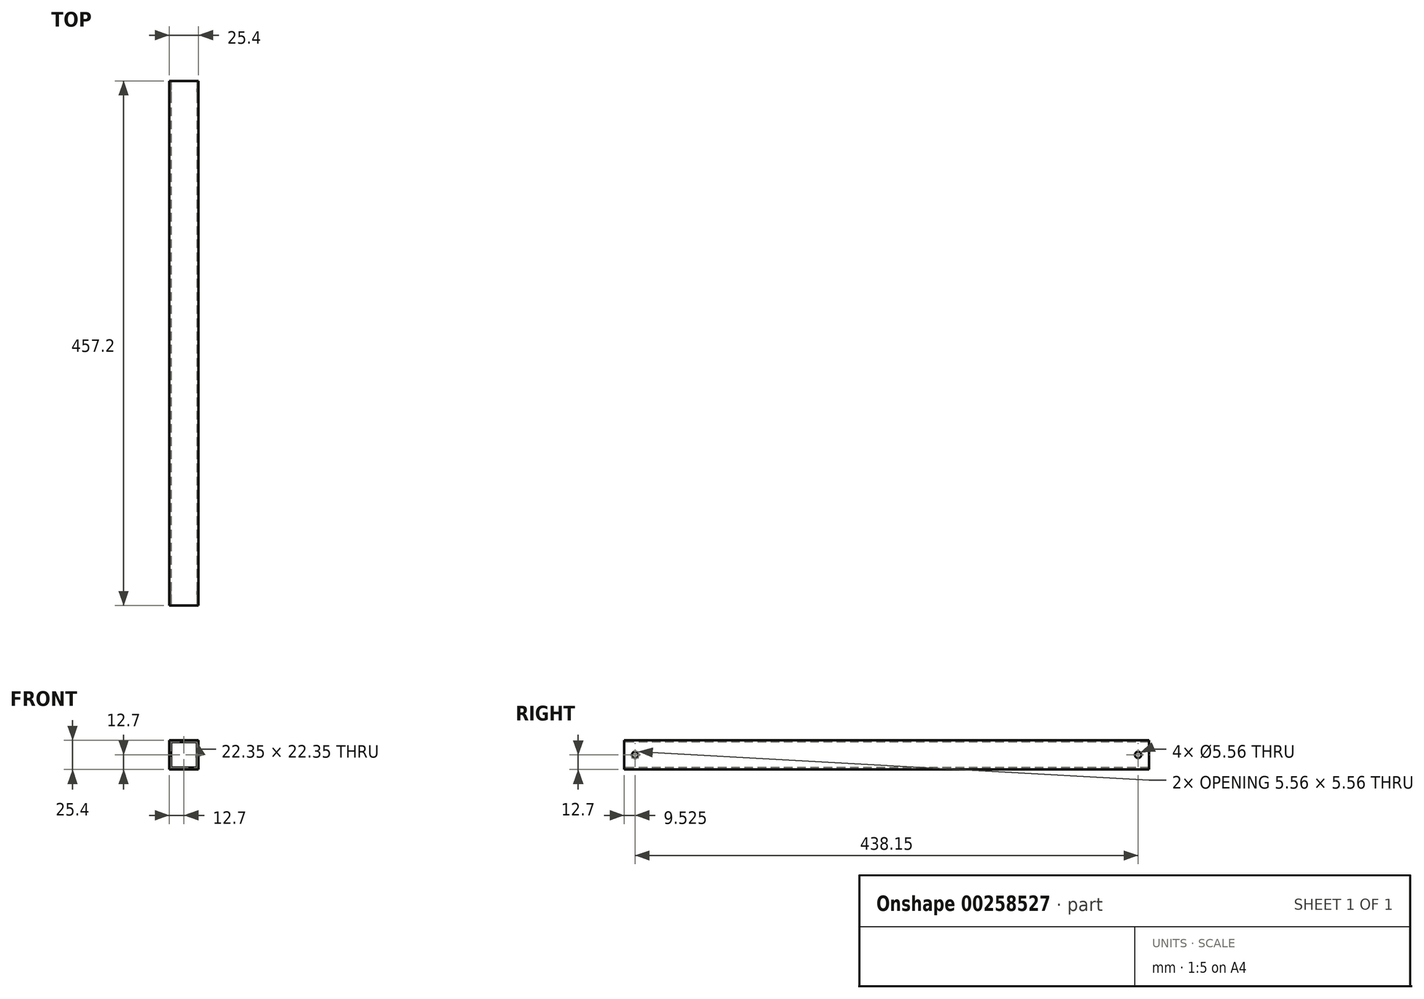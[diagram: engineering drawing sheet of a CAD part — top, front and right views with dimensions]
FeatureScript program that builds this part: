
annotation { "Feature Type Name" : "Feature", "Feature Type Description" : "" }
export const myFeature = defineFeature(function(context is Context, id is Id, definition is map)
    precondition{}
    {
        {
            var Q0;
            Q0=qCreatedBy(makeId("Front.planeOp"),FACE);
            var sketch = newSketch(context, id + "F0", { "sketchPlane" : qUnion([Q0])});
            skLineSegment(sketch, "E0.bottom", {"start": v(12.7, 12.7) * mm, "end": v(-12.7, 12.7) * mm});
            skLineSegment(sketch, "E0.top", {"start": v(12.7, -12.7) * mm, "end": v(-12.7, -12.7) * mm});
            skLineSegment(sketch, "E0.left", {"start": v(12.7, 12.7) * mm, "end": v(12.7, -12.7) * mm});
            skLineSegment(sketch, "E0.right", {"start": v(-12.7, 12.7) * mm, "end": v(-12.7, -12.7) * mm});
            skPoint(sketch, "E0.middle", {"position": v(0, 0) * mm});
            skLineSegment(sketch, "E1.0", {"start": v(11.18, 11.18) * mm, "end": v(-11.18, 11.18) * mm});
            skLineSegment(sketch, "E2.0", {"start": v(11.18, 11.18) * mm, "end": v(11.18, -11.18) * mm});
            skLineSegment(sketch, "E3.0", {"start": v(-11.18, 11.18) * mm, "end": v(-11.18, -11.18) * mm});
            skLineSegment(sketch, "E4.0", {"start": v(11.18, -11.18) * mm, "end": v(-11.18, -11.18) * mm});
            skSolve(sketch);
        }
        {
            var Q0;
            Q0 = qSketchRegion(id + "F0", true);
            extrude(context, id + "F1", {"entities" : qUnion([Q0]), "oppositeDirection" : true, "depth" : 457.2 * mm});
        }
        {
            var Q0;
            Q0=makeQuery(id+"F1.opExtrude","SWEPT_FACE",FACE,{"disambiguationData":[OSD([sQuery(id+"F0.wireOp",EDGE,"E0.left")])]});
            var sketch = newSketch(context, id + "F2", { "sketchPlane" : qUnion([Q0])});
            skCircle(sketch, "E5", {"center": v(9.53, 0) * mm, "radius": 2.78 * mm});
            skSolve(sketch);
        }
        {
            var Q0;
            Q0 = qSketchRegion(id + "F2", true);
            extrude(context, id + "F3", {"entities" : qUnion([Q0]), "operationType" : NewBodyOperationType.REMOVE, "oppositeDirection" : true, "depth" : 25.4 * mm});
        }
        {
            var Q0;
            Q0=makeQuery(id+"F1.opExtrude","SWEPT_FACE",FACE,{"disambiguationData":[OSD([sQuery(id+"F0.wireOp",EDGE,"E0.left")])]});
            var sketch = newSketch(context, id + "F4", { "sketchPlane" : qUnion([Q0])});
            skPoint(sketch, "E6.endSnap0", {"position": v(457.2, 0) * mm});
            skCircle(sketch, "E7", {"center": v(447.68, 0) * mm, "radius": 2.78 * mm});
            skPoint(sketch, "E6.start.orphan", {"position": v(457.2, 0) * mm});
            skSolve(sketch);
        }
        {
            var Q0;
            Q0 = qSketchRegion(id + "F4", true);
            extrude(context, id + "F5", {"entities" : qUnion([Q0]), "operationType" : NewBodyOperationType.REMOVE, "oppositeDirection" : true, "depth" : 25.4 * mm});
        }
    });
